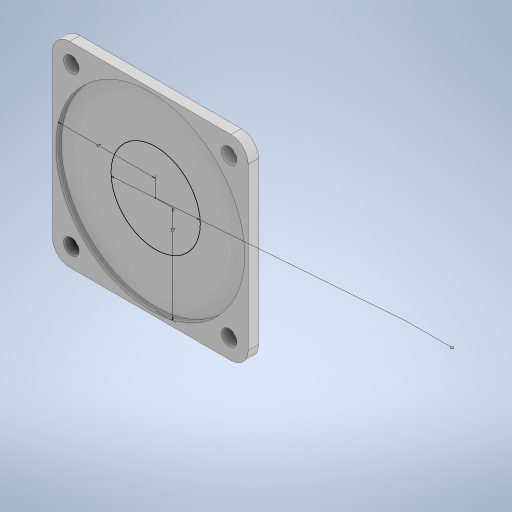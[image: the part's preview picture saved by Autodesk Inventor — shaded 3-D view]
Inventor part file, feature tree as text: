
AUTODESK INVENTOR PART (.ipt)
format: ipt  version: 2024 (Build 280153000, 153)  size: 290,304 bytes
history: native  units: in
note: dims shown in document units (in); Inventor stores cm internally (conversion verified against a paired STEP export)
features: sketch x4, extrude x3, fillet x2
ambient origin geometry x8: Origin, YZ Plane, XZ Plane, XY Plane, X Axis, Y Axis, Z Axis, Center Point
bodies: Solid1 (feature_tree)
feature tree (9):
  extrude  "Extrusion1"  Depth=4.4882in
  extrude  "Extrusion2"  Depth=0.2362in
  fillet  "Fillet1"  Radius=2.2441in
  fillet  "Fillet2"  Radius=2.2441in
  extrude  "Extrusion3"  Depth=0.3937in
  sketch  "Sketch4"  dims[d10=0.3937in d11=0.3543in d12=0.4346in d13=0.4346in d14=0.3543in d15=0.3543in d16=0.3543in d17=0.4346in d18=0.4346in d19=0.4346in d20=0.4346in d21=0.4346in d22=0.4346in d23=0.2362in d24=0.0in d25=2.0472in d26=2.2441in d27=2.2441in d28=0.0197in d29=0.0344in d30=0.0197in d31=0.0344in]
  sketch  "Sketch1"  dims[d0=4.4882in d1=4.4882in]
  sketch  "Sketch2"  dims[d2=0.2362in d3=0.0in d4=4.3307in d5=2.2441in d6=2.2441in]
  sketch  "Sketch3"  dims[d7=0.1181in d8=0.0in d9=0.3937in]
